# Revit family: PurePress Flush Plate
name_source: partatom
category: Plumbing Fixtures
units: mm (PartAtom-declared; Revit-internal decimal feet)

## family parameters
Always vertical = Yes
Cut with Voids When Loaded = No
Enable Cutting in Views = No
Maintain Annotation Orientation = No
OmniClass Number = 23.45.00.00
OmniClass Title = Sanitary, Laundry, and Cleaning Equipment
Part Type = Normal
Room Calculation Point = No
Round Connector Dimension = Use Diameter
Shared = No
Work Plane-Based = No

## types (3) — shared parameters
Category = Concealed Cistern
Fixing Details = https://www.lecicosa.co.za
Manufacturer = Lecico SA
Material = ABS Plastic
Model = Lecico Flush Plate Only
Technical Dimensions = W245 x H165 x D12mm
URL = https://www.lecicosa.co.za
zero-valued in all types: Default Elevation

## per-type parameters (varying)
| type | ABS Colour | Colour | Product Code |
| Lecico Flush Plate - White | White | White | LECFLUPLA0WHIBC |
| Lecico Flush Plate - Black | Black | Black | LECFLUPLA0BLABC |
| Lecico Flush Plate - Chrome | Silver | Chrome | LECFLUPLA0CHRBC |

## geometry (parser evidence)
native form markers: Sweep x3
no freeform markers — native parametric forms only
